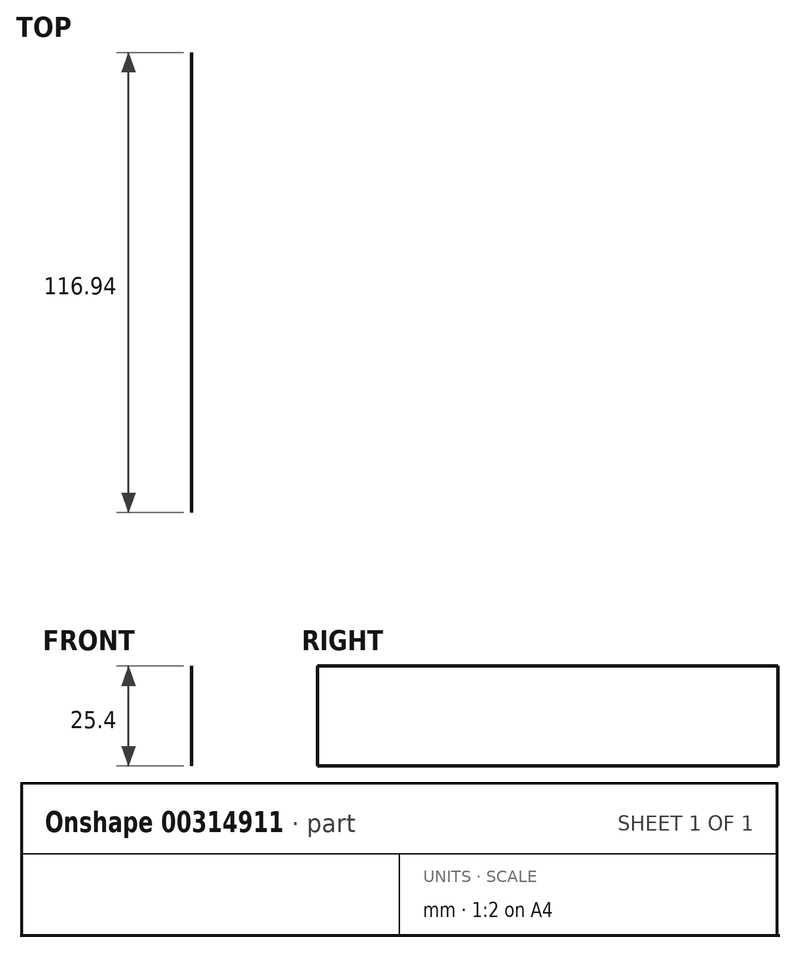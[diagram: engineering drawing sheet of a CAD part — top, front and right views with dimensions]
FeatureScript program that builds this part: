
annotation { "Feature Type Name" : "Feature", "Feature Type Description" : "" }
export const myFeature = defineFeature(function(context is Context, id is Id, definition is map)
    precondition{}
    {
        {
            var Q0;
            Q0=qCreatedBy(makeId("Top.planeOp"),FACE);
            var sketch = newSketch(context, id + "F0", { "sketchPlane" : qUnion([Q0])});
            skLineSegment(sketch, "E0.bottom", {"start": v(0, 0) * mm, "end": v(119.44, 0) * mm});
            skLineSegment(sketch, "E0.top", {"start": v(0, 116.94) * mm, "end": v(119.44, 116.94) * mm});
            skLineSegment(sketch, "E0.left", {"start": v(0, 0) * mm, "end": v(0, 116.94) * mm});
            skLineSegment(sketch, "E0.right", {"start": v(119.44, 0) * mm, "end": v(119.44, 116.94) * mm});
            skSolve(sketch);
        }
        {
            var Q0;
            Q0=sQuery(id+"F0.wireOp",EDGE,"E0.right");
            extrude(context, id + "F1", {"bodyType" : ToolBodyType.SURFACE, "surfaceEntities" : qUnion([Q0]), "depth" : 25.4 * mm});
        }
    });
